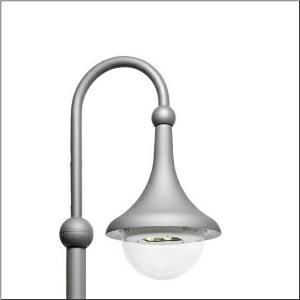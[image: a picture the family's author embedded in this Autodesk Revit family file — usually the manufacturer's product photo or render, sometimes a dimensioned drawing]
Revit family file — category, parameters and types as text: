
# Revit family: kleine_glocke_iq___st1_2a_5xa1575e1f108_8dd9
name_source: partatom
category: Lighting Fixtures
units: mm (PartAtom-declared; Revit-internal decimal feet)

## family parameters
Cut with Voids When Loaded = No
Host = Face
Light Source = No
Part Type = Normal
Room Calculation Point = No
Round Connector Dimension = Use Diameter
Shared = No

## types (1)
- --- (1 x LED, 3220 lm, 20.1 W, 3000K)
    Apparent Load = 20 VA
    CIE Flux Codes = 28 65 95 100 100
    Color Rendering = 70
    Color Temperature = 3000K
    Default Elevation = 1800 mm
    Description = Small Bell iQ, mast luminaire, primary light control with 3 zone facetted reflector, of plastic, silver coated, primary optical cover: enclosure, of PMMA, transparent, light distribution: ST1.2a, light emission: direct distribution, primary light characteristic: asymmetric, installation type: suspended mounting, LED, High Power LED, rated luminous flux: 3.220lm, luminous efficacy: 160lm/W, light colour: 730, colour temperature: 3000K, control gear: iQ Street-Remote, control: optimised constant luminous flux control (CLO 2.0), Desk-Remote (wireless, voltage-free reading and setting of iQ features in the workshop via application-optimized NFC function/RFID function), Light-Fading, Smart-Wire, Night-Set, Lumen-Switch, Temp-Guard, Auto-Match, Street-Remote, pre-setting: logarithmic dimming characteristic, mains connection: 230..240V, AC, 50/60Hz, start of lifetime: 20W, end of service life: 21W, reduction: 10W, luminaire housing, bell-shaped, of glass-fibre reinforced polyester, coated, Siteco® metallic grey (DB 702S), please order curved mast extension separately, diameter: 430mm, height: 575mm, mounting height: 2.5..4.0m, protection rating (complete): IP54, insulation class (complete): insulation class II (safety insulation), certification: CE, ENEC, VDE, impact resistance: IK09, standard-compliant lighting for roads and squares, packaging unit: 1 piece

Light Distribution: ST1.2a
    Height = 575 mm
    Lamp = 1 x LED
    Lamp Light Flux = 3220 lm
    Lamp Power = 20.1 W
    Lamp count = 1
    Length = 430 mm
    Luminous efficacy = 160 lm/W
    Manufacturer = Siteco
    ModVariant = No
    Model = 5XA1575E1F108
    Number of Poles = 1
    OnlyDefault = Yes
    Power Factor = 1
    Product Name = Kleine Glocke iQ | ST1.2a
    Product group = mast luminaire | pylon annexe
    ProductGroupID = 6200
    Protection Class = Protection class II
    Protection Degree = IP 54
    RLX_Detail_Level = 1
    RLX_Emergency_Light_Flux = 0 lm
    RLX_Emergency_Type = 0
    RLX_Emergency_Type_DB = No
    RlxData = <blob elided: 56449 chars, md5=165897d6>
    Socket = socket
    Standby Power = 0 W
    System Light Flux = 3220 lm
    System Power = 20 W
    Type Comments = factory setting: luminous flux: 100 % | dim-lin: 254 | 376 mA
    Type Image = l_1347699.jpg
    URL = http://relux.com
    VarID = @adj_008833
    Voltage = 0 V
    Weight = 0.00 kg
    Width = 0 mm  [stored 0 ft]

note: [stored X ft] marks values corroborated as IEEE doubles in the binary element streams (Revit-internal decimal feet)

## geometry (parser evidence)
native form markers: Blend x4, Sweep x9
no freeform markers — native parametric forms only
